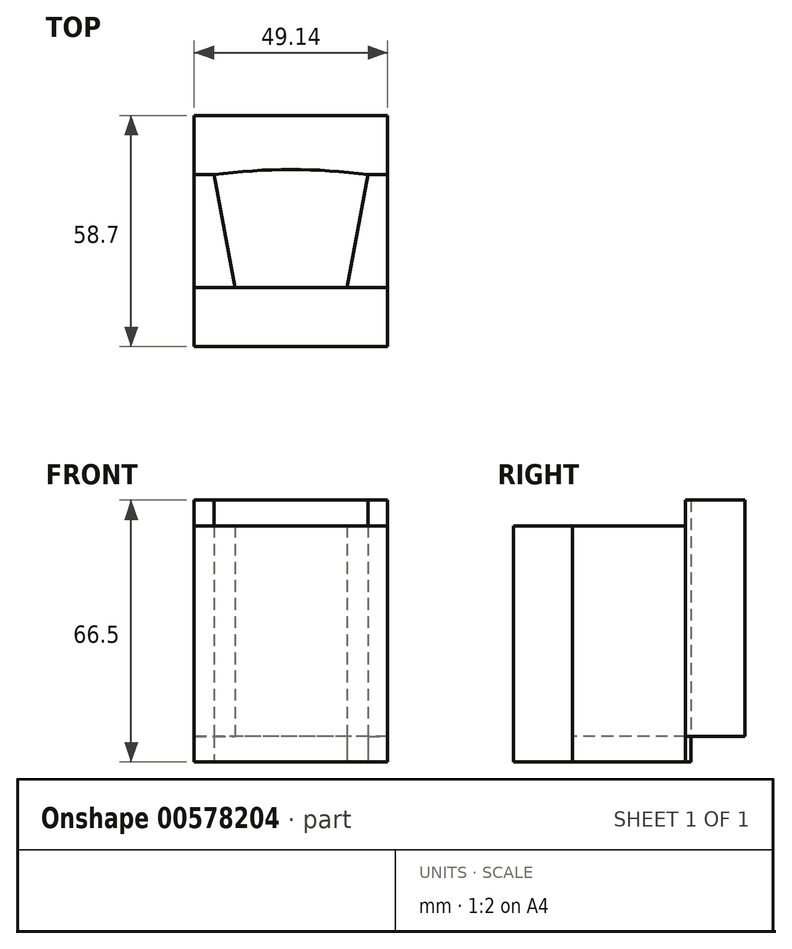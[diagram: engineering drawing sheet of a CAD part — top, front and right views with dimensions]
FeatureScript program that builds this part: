
annotation { "Feature Type Name" : "Feature", "Feature Type Description" : "" }
export const myFeature = defineFeature(function(context is Context, id is Id, definition is map)
    precondition{}
    {
        {
            var Q0;
            Q0=qCreatedBy(makeId("Top.planeOp"),FACE);
            var sketch = newSketch(context, id + "F0", { "sketchPlane" : qUnion([Q0])});
            skLineSegment(sketch, "E0.bottom", {"start": v(14.26, -15) * mm, "end": v(-14.26, -15) * mm});
            skPoint(sketch, "E0.middle", {"position": v(0, 0) * mm});
            skArc(sketch, "E1", {"start": v(19.57, 13.7) * mm, "mid": v(0, 15) * mm, "end": v(-19.57, 13.7) * mm});
            skLineSegment(sketch, "E2", {"start": v(-19.57, 13.7) * mm, "end": v(-14.26, -15) * mm});
            skLineSegment(sketch, "E3", {"start": v(19.58, 13.7) * mm, "end": v(14.26, -15) * mm});
            skPoint(sketch, "E4.orphan", {"position": v(-19.57, -15) * mm});
            skPoint(sketch, "E5.orphan", {"position": v(19.58, -15) * mm});
            skPoint(sketch, "E0.right.end.orphan", {"position": v(-19.57, 15) * mm});
            skPoint(sketch, "E0.left.end.orphan", {"position": v(19.57, 15) * mm});
            skSolve(sketch);
        }
        {
            var Q0;
            Q0 = qSketchRegion(id + "F0", true);
            extrude(context, id + "F1", {"entities" : qUnion([Q0]), "depth" : 6.5 * mm, "offsetDistance" : 25 * mm});
        }
        {
            var Q0;
            Q0=makeQuery(id+"F1.opExtrude","CAP_FACE",FACE,{"disambiguationData":[OSD([sQuery(id+"F0.wireOp",EDGE,"E0.bottom"),sQuery(id+"F0.wireOp",EDGE,"E1"),sQuery(id+"F0.wireOp",EDGE,"E2"),sQuery(id+"F0.wireOp",EDGE,"E3")])],"isStart":true});
            var sketch = newSketch(context, id + "F2", { "sketchPlane" : qUnion([Q0])});
            skLineSegment(sketch, "E6", {"start": v(-19.57, 15) * mm, "end": v(-14.26, 15) * mm});
            skLineSegment(sketch, "E7", {"start": v(-14.26, 15) * mm, "end": v(-19.57, -13.7) * mm});
            skLineSegment(sketch, "E8.bottom", {"start": v(-19.57, -13.7) * mm, "end": v(-24.57, -13.7) * mm});
            skLineSegment(sketch, "E8.top", {"start": v(-19.57, 15) * mm, "end": v(-24.57, 15) * mm});
            skLineSegment(sketch, "E8.right", {"start": v(-24.57, -13.7) * mm, "end": v(-24.58, 15) * mm});
            skSolve(sketch);
        }
        {
            var Q0;
            Q0 = qSketchRegion(id + "F2", true);
            extrude(context, id + "F3", {"entities" : qUnion([Q0]), "oppositeDirection" : true, "depth" : 60 * mm, "offsetDistance" : 25 * mm});
        }
        {
            var Q0;
            Q0=makeQuery(id+"F3.opExtrude","SWEPT_BODY",BODY,{"disambiguationData":[OSD([sQuery(id+"F2.wireOp",EDGE,"E6"),sQuery(id+"F2.wireOp",EDGE,"E7"),sQuery(id+"F2.wireOp",EDGE,"E8.bottom"),sQuery(id+"F2.wireOp",EDGE,"E8.top"),sQuery(id+"F2.wireOp",EDGE,"E8.right")])]});
            var Q1;
            Q1=qCreatedBy(makeId("Right.planeOp"),FACE);
            mirror(context, id + "F4", {"operationType" : NewBodyOperationType.ADD, "entities" : qUnion([Q0]), "mirrorPlane" : qUnion([Q1])});
        }
        {
            var Q0;
            Q0=makeQuery(id+"F1.opExtrude","CAP_FACE",FACE,{"disambiguationData":[OSD([sQuery(id+"F0.wireOp",EDGE,"E0.bottom"),sQuery(id+"F0.wireOp",EDGE,"E1"),sQuery(id+"F0.wireOp",EDGE,"E2"),sQuery(id+"F0.wireOp",EDGE,"E3")])],"isStart":false});
            var sketch = newSketch(context, id + "F5", { "sketchPlane" : qUnion([Q0])});
            skArc(sketch, "E9", {"start": v(19.57, 13.7) * mm, "mid": v(0, 15) * mm, "end": v(-19.57, 13.7) * mm});
            skLineSegment(sketch, "E10", {"start": v(19.57, 13.7) * mm, "end": v(24.57, 13.7) * mm});
            skLineSegment(sketch, "E11", {"start": v(24.57, 13.7) * mm, "end": v(24.57, 28.7) * mm});
            skLineSegment(sketch, "E12", {"start": v(24.57, 28.7) * mm, "end": v(-24.57, 28.7) * mm});
            skLineSegment(sketch, "E13", {"start": v(-24.57, 28.7) * mm, "end": v(-24.57, 13.7) * mm});
            skLineSegment(sketch, "E14", {"start": v(-24.57, 13.7) * mm, "end": v(-19.57, 13.7) * mm});
            skSolve(sketch);
        }
        {
            var Q0;
            Q0 = qSketchRegion(id + "F5", true);
            extrude(context, id + "F6", {"entities" : qUnion([Q0]), "depth" : 60 * mm, "offsetDistance" : 25 * mm});
        }
        {
            var Q0;
            Q0=makeQuery(id+"F3.opExtrude","CAP_FACE",FACE,{"disambiguationData":[OSD([sQuery(id+"F2.wireOp",EDGE,"E6"),sQuery(id+"F2.wireOp",EDGE,"E7"),sQuery(id+"F2.wireOp",EDGE,"E8.bottom"),sQuery(id+"F2.wireOp",EDGE,"E8.top"),sQuery(id+"F2.wireOp",EDGE,"E8.right")])],"isStart":false});
            var sketch = newSketch(context, id + "F7", { "sketchPlane" : qUnion([Q0])});
            skLineSegment(sketch, "E15.bottom", {"start": v(-24.57, -15) * mm, "end": v(24.58, -15) * mm});
            skLineSegment(sketch, "E15.top", {"start": v(-24.57, -30) * mm, "end": v(24.58, -30) * mm});
            skLineSegment(sketch, "E15.left", {"start": v(-24.57, -15) * mm, "end": v(-24.57, -30) * mm});
            skLineSegment(sketch, "E15.right", {"start": v(24.58, -15) * mm, "end": v(24.58, -30) * mm});
            skSolve(sketch);
        }
        {
            var Q0;
            Q0 = qSketchRegion(id + "F7", true);
            extrude(context, id + "F8", {"entities" : qUnion([Q0]), "oppositeDirection" : true, "depth" : 60 * mm, "offsetDistance" : 25 * mm});
        }
    });
